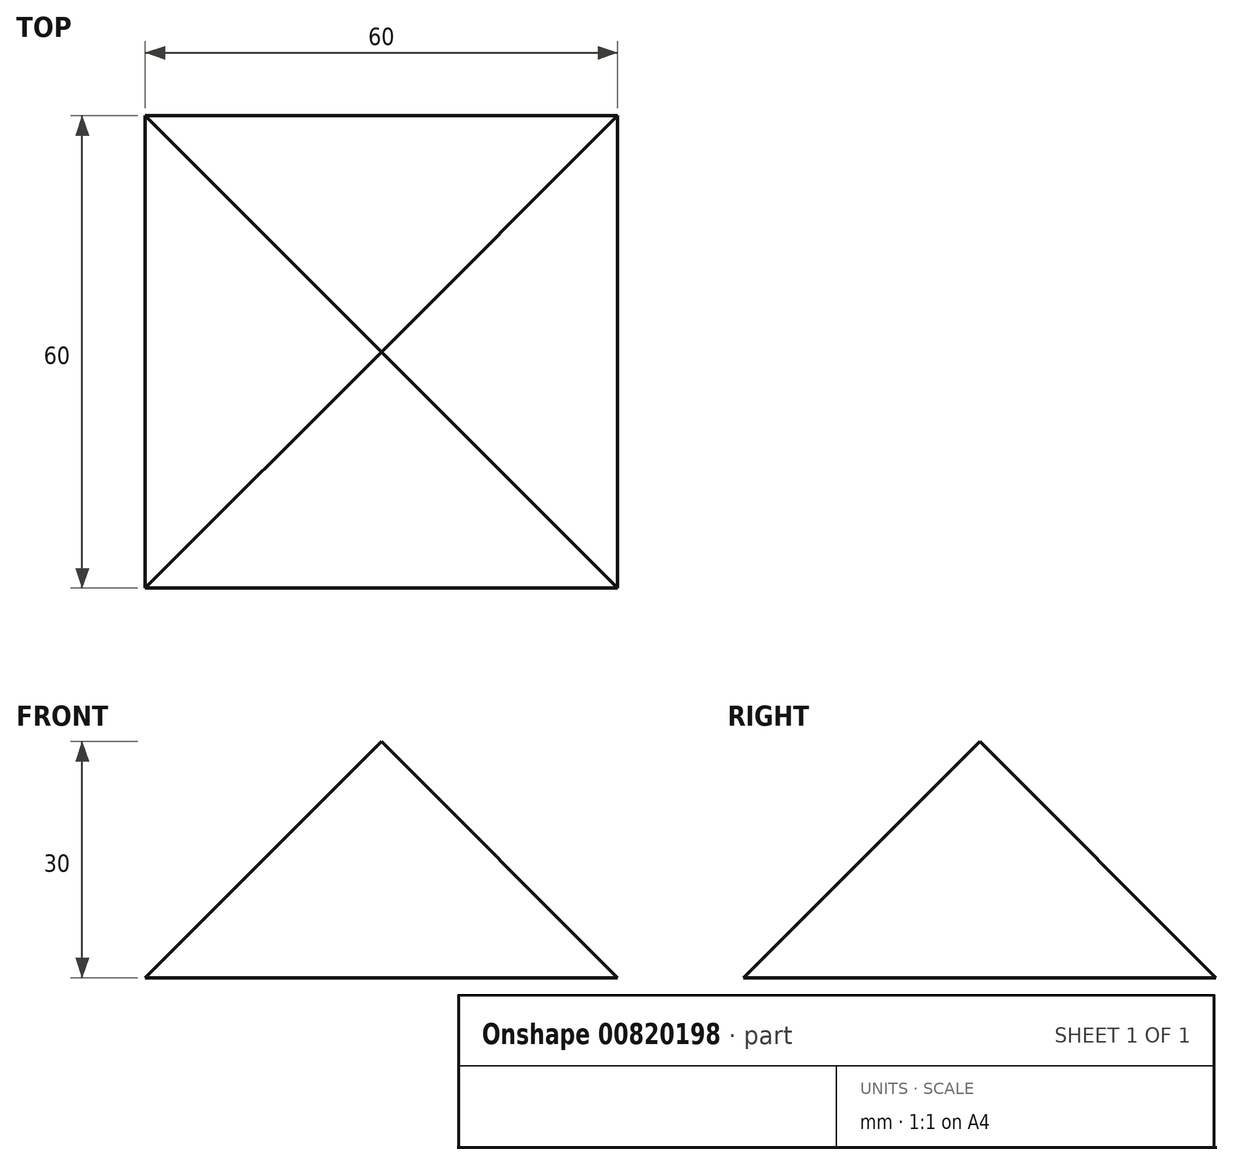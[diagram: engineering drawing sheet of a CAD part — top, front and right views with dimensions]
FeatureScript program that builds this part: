
annotation { "Feature Type Name" : "Feature", "Feature Type Description" : "" }
export const myFeature = defineFeature(function(context is Context, id is Id, definition is map)
    precondition{}
    {
        {
            var Q0;
            Q0=qCreatedBy(makeId("Top.planeOp"),FACE);
            var sketch = newSketch(context, id + "F0", { "sketchPlane" : qUnion([Q0])});
            skLineSegment(sketch, "E0.bottom", {"start": v(-30, 30) * mm, "end": v(30, 30) * mm});
            skLineSegment(sketch, "E0.top", {"start": v(-30, -30) * mm, "end": v(30, -30) * mm});
            skLineSegment(sketch, "E0.left", {"start": v(-30, 30) * mm, "end": v(-30, -30) * mm});
            skLineSegment(sketch, "E0.right", {"start": v(30, 30) * mm, "end": v(30, -30) * mm});
            skPoint(sketch, "E0.middle", {"position": v(0, 0) * mm});
            skSolve(sketch);
        }
        {
            var Q0;
            Q0 = qSketchRegion(id + "F0", true);
            extrude(context, id + "F1", {"entities" : qUnion([Q0]), "depth" : 30 * mm, "offsetDistance" : 25.4 * mm, "hasDraft" : true, "draftAngle" : 45 * degree, "draftPullDirection" : true});
        }
    });
